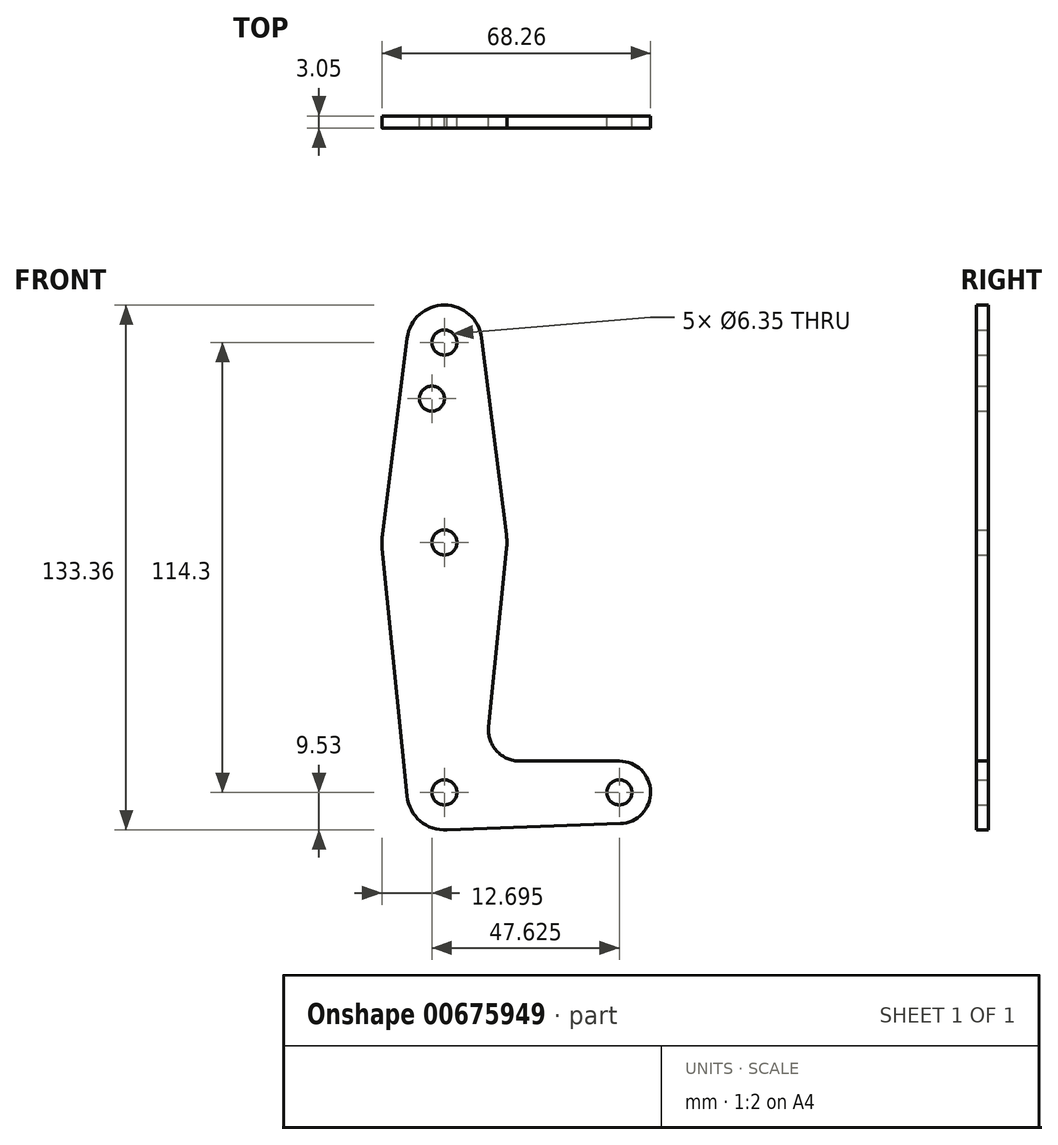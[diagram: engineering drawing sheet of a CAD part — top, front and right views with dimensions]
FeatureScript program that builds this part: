
annotation { "Feature Type Name" : "Feature", "Feature Type Description" : "" }
export const myFeature = defineFeature(function(context is Context, id is Id, definition is map)
    precondition{}
    {
        {
            var Q0;
            Q0=qCreatedBy(makeId("Front.planeOp"),FACE);
            var sketch = newSketch(context, id + "F0", { "sketchPlane" : qUnion([Q0])});
            skCircle(sketch, "E0", {"center": v(44.45, 0) * mm, "radius": 7.94 * mm});
            skCircle(sketch, "E1", {"center": v(0, 63.5) * mm, "radius": 15.88 * mm});
            skCircle(sketch, "E2", {"center": v(0, 114.3) * mm, "radius": 9.53 * mm});
            skLineSegment(sketch, "E3", {"start": v(0, 0) * mm, "end": v(44.45, 0) * mm, "construction": true});
            skLineSegment(sketch, "E4", {"start": v(0, 0) * mm, "end": v(0, 63.5) * mm, "construction": true});
            skLineSegment(sketch, "E5", {"start": v(0, 114.3) * mm, "end": v(0, 63.5) * mm, "construction": true});
            skCircle(sketch, "E6", {"center": v(0, 0) * mm, "radius": 9.53 * mm});
            skLineSegment(sketch, "E7", {"start": v(44.73, -7.93) * mm, "end": v(0, -9.53) * mm});
            skLineSegment(sketch, "E8", {"start": v(-9.45, 115.5) * mm, "end": v(-15.75, 65.48) * mm});
            skLineSegment(sketch, "E9", {"start": v(9.45, 115.5) * mm, "end": v(15.75, 65.48) * mm});
            skCircle(sketch, "E10", {"center": v(0, 114.3) * mm, "radius": 3.18 * mm});
            skCircle(sketch, "E11", {"center": v(0, 0) * mm, "radius": 3.18 * mm});
            skCircle(sketch, "E12", {"center": v(44.45, 0) * mm, "radius": 3.18 * mm});
            skCircle(sketch, "E13", {"center": v(0, 63.5) * mm, "radius": 3.18 * mm});
            skCircle(sketch, "E14", {"center": v(-3.17, 100.03) * mm, "radius": 3.18 * mm});
            skLineSegment(sketch, "E15", {"start": v(15.8, 61.91) * mm, "end": v(11.25, 16.68) * mm});
            skLineSegment(sketch, "E16", {"start": v(44.45, 7.94) * mm, "end": v(19.16, 7.94) * mm});
            skArc(sketch, "E17.filletArc", {"start": v(11.25, 16.68) * mm, "mid": v(13.26, 10.55) * mm, "end": v(19.16, 7.94) * mm});
            skLineSegment(sketch, "E18", {"start": v(-15.8, 61.91) * mm, "end": v(-9.48, -0.95) * mm});
            skSolve(sketch);
        }
        {
            var Q0;
            Q0 = qSketchRegion(id + "F0", true);
            extrude(context, id + "F1", {"entities" : qUnion([Q0]), "depth" : 3.05 * mm, "offsetDistance" : 25.4 * mm});
        }
    });
